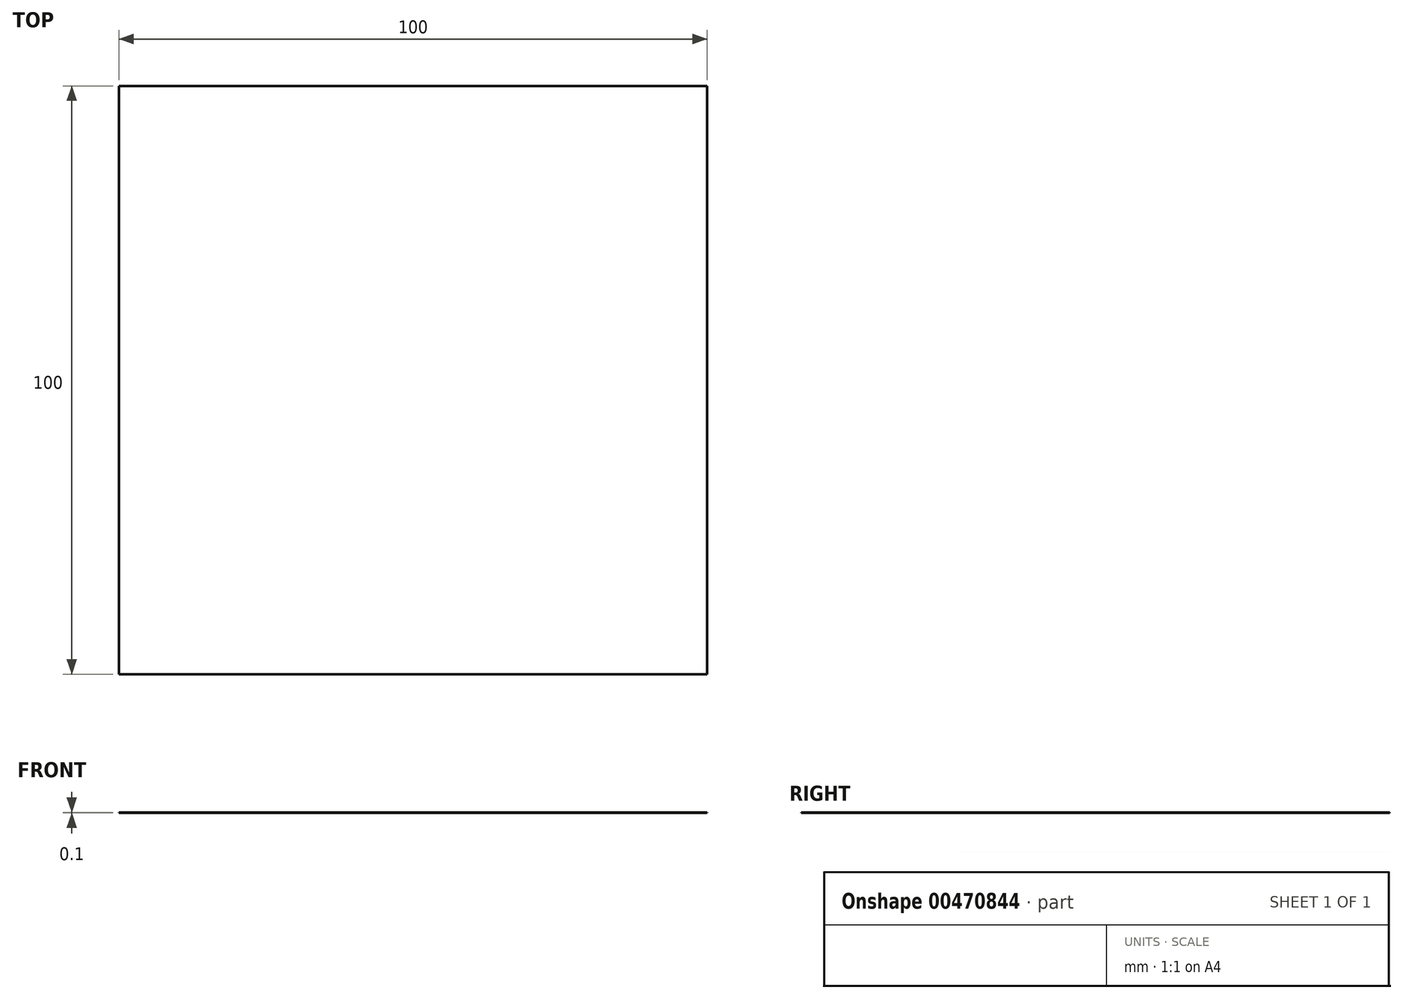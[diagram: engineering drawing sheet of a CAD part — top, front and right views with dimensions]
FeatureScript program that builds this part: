
annotation { "Feature Type Name" : "Feature", "Feature Type Description" : "" }
export const myFeature = defineFeature(function(context is Context, id is Id, definition is map)
    precondition{}
    {
        {
            var Q0;
            Q0=qCreatedBy(makeId("Top.planeOp"),FACE);
            var sketch = newSketch(context, id + "F0", { "sketchPlane" : qUnion([Q0])});
            skLineSegment(sketch, "E0.bottom", {"start": v(-86.57, 62.67) * mm, "end": v(13.43, 62.67) * mm});
            skLineSegment(sketch, "E0.top", {"start": v(-86.57, -37.33) * mm, "end": v(13.43, -37.33) * mm});
            skLineSegment(sketch, "E0.left", {"start": v(-86.57, 62.67) * mm, "end": v(-86.57, -37.33) * mm});
            skLineSegment(sketch, "E0.right", {"start": v(13.43, 62.67) * mm, "end": v(13.43, -37.33) * mm});
            skSolve(sketch);
        }
        {
            var Q0;
            Q0=makeQuery(id+"F0.imprint","IMPRINT",FACE,{"disambiguationData":[TD([[makeQuery(id+"F0.imprint","IMPRINT",EDGE,{"derivedFrom":sQuery(id+"F0.wireOp",EDGE,"E0.bottom")}),-1.0]])]});
            extrude(context, id + "F1", {"entities" : qUnion([Q0]), "depth" : 0.1 * mm});
        }
    });
